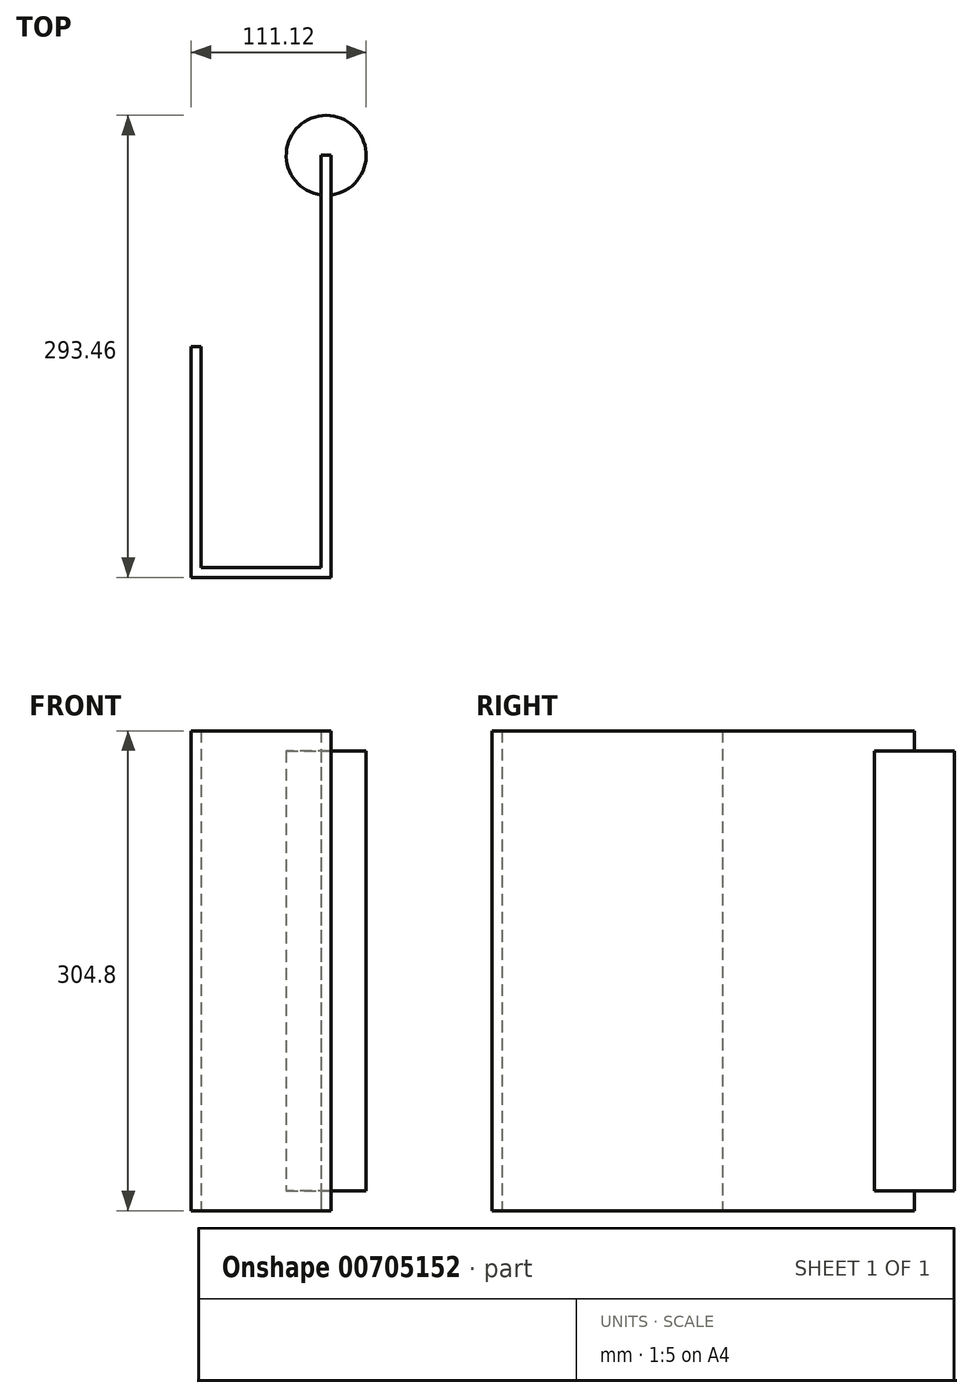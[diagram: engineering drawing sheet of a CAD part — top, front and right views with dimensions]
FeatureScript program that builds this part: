
annotation { "Feature Type Name" : "Feature", "Feature Type Description" : "" }
export const myFeature = defineFeature(function(context is Context, id is Id, definition is map)
    precondition{}
    {
        {
            var Q0;
            Q0=qCreatedBy(makeId("Top.planeOp"),FACE);
            var sketch = newSketch(context, id + "F0", { "sketchPlane" : qUnion([Q0])});
            skLineSegment(sketch, "E0", {"start": v(11.18, 0) * mm, "end": v(11.18, 268.06) * mm});
            skLineSegment(sketch, "E1", {"start": v(4.83, 268.06) * mm, "end": v(11.18, 268.06) * mm});
            skLineSegment(sketch, "E2", {"start": v(4.83, 6.35) * mm, "end": v(4.83, 268.06) * mm});
            skLineSegment(sketch, "E3", {"start": v(-71.37, 6.35) * mm, "end": v(4.83, 6.35) * mm});
            skLineSegment(sketch, "E4", {"start": v(-71.37, 146.4) * mm, "end": v(-71.37, 6.35) * mm});
            skLineSegment(sketch, "E5", {"start": v(-77.72, 146.4) * mm, "end": v(-71.37, 146.4) * mm});
            skLineSegment(sketch, "E6", {"start": v(-77.72, 0) * mm, "end": v(-77.72, 146.4) * mm});
            skLineSegment(sketch, "E7", {"start": v(11.18, 0) * mm, "end": v(-77.72, 0) * mm});
            skCircle(sketch, "E8", {"center": v(8, 268.06) * mm, "radius": 25.4 * mm});
            skSolve(sketch);
        }
        {
            var Q0;
            {var subQ0=sQuery(id+"F0.wireOp",EDGE,"E3");Q0=makeQuery(id+"F0.imprint","IMPRINT",FACE,{"disambiguationData":[TD([[makeQuery(id+"F0.imprint","IMPRINT",EDGE,{"derivedFrom":subQ0}),-1.0]])]});}
            var Q1;
            {var subQ0=sQuery(id+"F0.wireOp",EDGE,"E1");Q1=makeQuery(id+"F0.imprint","IMPRINT",FACE,{"disambiguationData":[TD([[makeQuery(id+"F0.imprint","IMPRINT",EDGE,{"derivedFrom":subQ0}),-1.0]])]});}
            extrude(context, id + "F1", {"entities" : qUnion([Q0, Q1]), "endBound" : BoundingType.SYMMETRIC, "depth" : 304.8 * mm, "offsetDistance" : 25.4 * mm});
        }
        {
            var Q0;
            {var subQ0=sQuery(id+"F0.wireOp",EDGE,"E1");Q0=makeQuery(id+"F0.imprint","IMPRINT",FACE,{"disambiguationData":[TD([[makeQuery(id+"F0.imprint","IMPRINT",EDGE,{"derivedFrom":subQ0}),1.0]])]});}
            extrude(context, id + "F2", {"entities" : qUnion([Q0]), "operationType" : NewBodyOperationType.ADD, "endBound" : BoundingType.SYMMETRIC, "depth" : 279.4 * mm, "offsetDistance" : 25.4 * mm});
        }
    });
